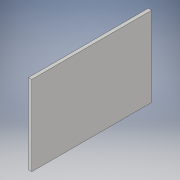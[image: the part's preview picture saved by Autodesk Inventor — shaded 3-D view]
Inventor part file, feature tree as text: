
AUTODESK INVENTOR PART (.ipt)
format: ipt  version: 2017 (Build 210142000, 142)  size: 86,528 bytes
history: native  units: in
note: dims shown in document units (in); Inventor stores cm internally (conversion verified against a paired STEP export)
features: extrude x1, sketch x1
ambient origin geometry x8: Origin, YZ Plane, XZ Plane, XY Plane, X Axis, Y Axis, Z Axis, Center Point
bodies: Solid1 (feature_tree)
feature tree (2):
  extrude  "Extrusion1"  Depth=36.0in
  sketch  "Sketch1"  dims[d0=24.0in d1=36.0in d2=1.0in d3=0.0in]
